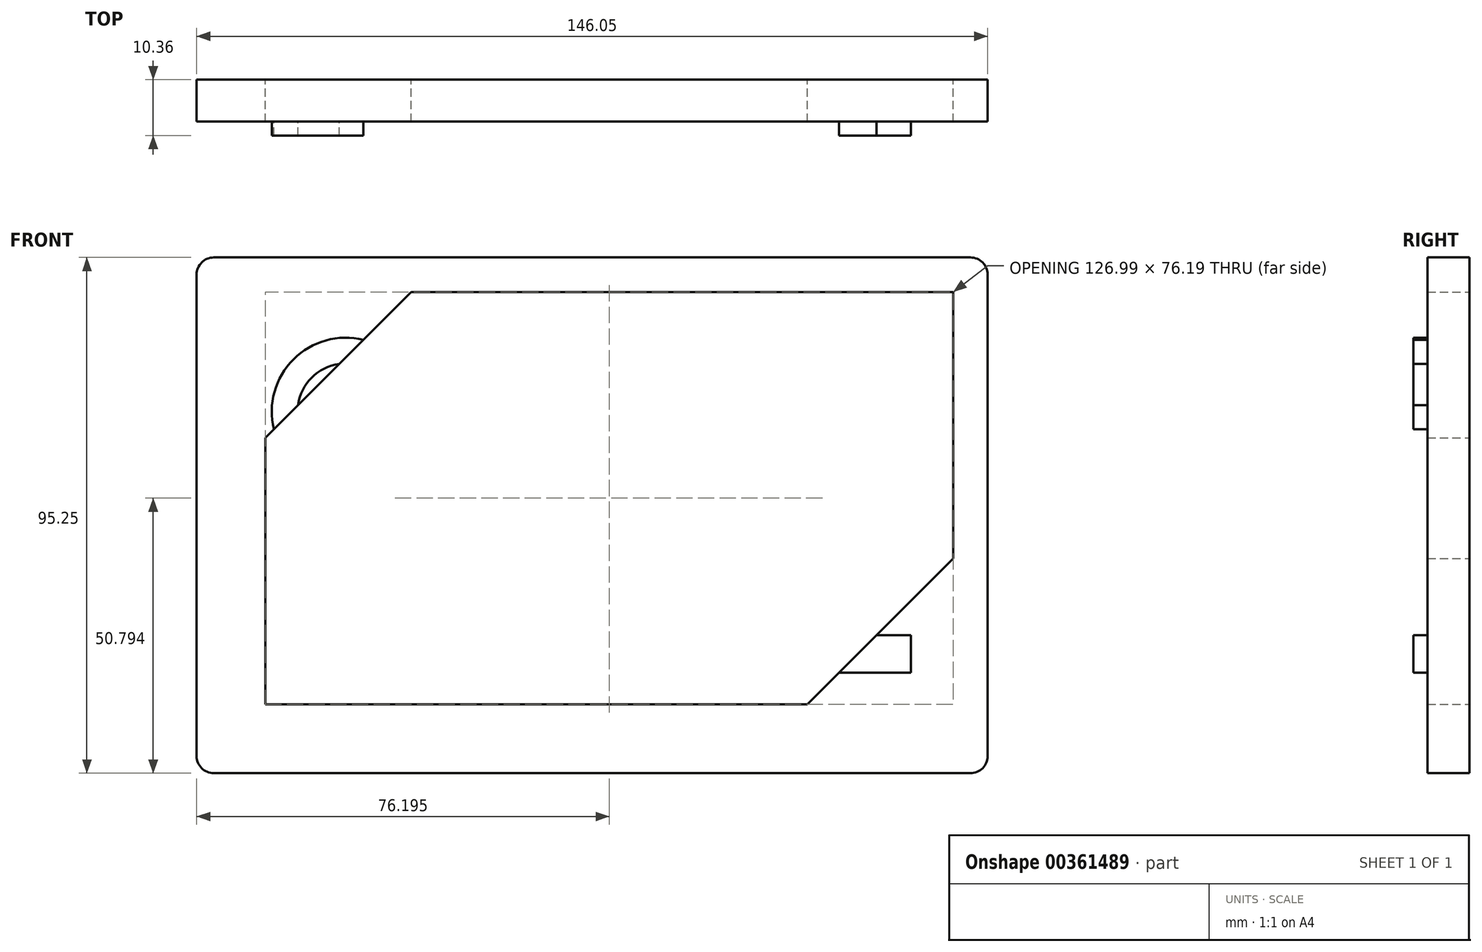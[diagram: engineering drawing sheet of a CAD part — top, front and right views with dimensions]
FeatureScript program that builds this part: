
annotation { "Feature Type Name" : "Feature", "Feature Type Description" : "" }
export const myFeature = defineFeature(function(context is Context, id is Id, definition is map)
    precondition{}
    {
        {
            var Q0;
            Q0=qCreatedBy(makeId("Front.planeOp"),FACE);
            var sketch = newSketch(context, id + "F0", { "sketchPlane" : qUnion([Q0])});
            skArc(sketch, "E0", {"start": v(-36.47, 6.36) * mm, "mid": v(-38.71, 5.43) * mm, "end": v(-39.64, 3.18) * mm});
            skArc(sketch, "E1", {"start": v(106.4, 3.18) * mm, "mid": v(105.48, 5.43) * mm, "end": v(103.23, 6.36) * mm});
            skArc(sketch, "E2", {"start": v(-39.64, -85.72) * mm, "mid": v(-38.71, -87.96) * mm, "end": v(-36.47, -88.9) * mm});
            skArc(sketch, "E3", {"start": v(103.23, -88.9) * mm, "mid": v(105.48, -87.96) * mm, "end": v(106.4, -85.72) * mm});
            skLineSegment(sketch, "E4", {"start": v(-39.64, 3.18) * mm, "end": v(-39.64, -85.72) * mm});
            skLineSegment(sketch, "E5", {"start": v(-36.47, -88.9) * mm, "end": v(103.23, -88.9) * mm});
            skLineSegment(sketch, "E6", {"start": v(106.4, -85.72) * mm, "end": v(106.4, 3.18) * mm});
            skLineSegment(sketch, "E7", {"start": v(-36.47, 6.36) * mm, "end": v(103.23, 6.36) * mm});
            skLineSegment(sketch, "E8", {"start": v(-26.94, -76.2) * mm, "end": v(73.1, -76.2) * mm});
            skLineSegment(sketch, "E9", {"start": v(73.1, -76.2) * mm, "end": v(100.05, -49.25) * mm});
            skLineSegment(sketch, "E10", {"start": v(100.05, -49.25) * mm, "end": v(100.05, 0) * mm});
            skLineSegment(sketch, "E11", {"start": v(100.05, 0) * mm, "end": v(0, 0) * mm});
            skLineSegment(sketch, "E12", {"start": v(0, 0) * mm, "end": v(-26.94, -26.94) * mm});
            skLineSegment(sketch, "E13", {"start": v(-26.94, -26.94) * mm, "end": v(-26.94, -76.2) * mm});
            skSolve(sketch);
        }
        {
            var Q0;
            {var subQ1=sQuery(id+"F0.wireOp",EDGE,"E0");Q0=makeQuery(id+"F0.imprint","IMPRINT",FACE,{"disambiguationData":[TD([[makeQuery(id+"F0.imprint","IMPRINT",EDGE,{"derivedFrom":subQ1}),1.0]])]});}
            extrude(context, id + "F1", {"entities" : qUnion([Q0]), "depth" : 7.77 * mm});
        }
        {
            var Q0;
            Q0=makeQuery(id+"F1.opExtrude","CAP_FACE",FACE,{"disambiguationData":[OSD([sQuery(id+"F0.wireOp",EDGE,"E0"),sQuery(id+"F0.wireOp",EDGE,"E1"),sQuery(id+"F0.wireOp",EDGE,"E2"),sQuery(id+"F0.wireOp",EDGE,"E3"),sQuery(id+"F0.wireOp",EDGE,"E4"),sQuery(id+"F0.wireOp",EDGE,"E5"),sQuery(id+"F0.wireOp",EDGE,"E6"),sQuery(id+"F0.wireOp",EDGE,"E7"),sQuery(id+"F0.wireOp",EDGE,"E8"),sQuery(id+"F0.wireOp",EDGE,"E9"),sQuery(id+"F0.wireOp",EDGE,"E10"),sQuery(id+"F0.wireOp",EDGE,"E11"),sQuery(id+"F0.wireOp",EDGE,"E12"),sQuery(id+"F0.wireOp",EDGE,"E13")])],"isStart":false});
            var sketch = newSketch(context, id + "F2", { "sketchPlane" : qUnion([Q0])});
            skCircle(sketch, "E14", {"center": v(-12.1, -22.12) * mm, "radius": 13.67 * mm});
            skCircle(sketch, "E15", {"center": v(-12.1, -22.12) * mm, "radius": 8.9 * mm});
            skLineSegment(sketch, "E16.bottom", {"start": v(85.9, -63.4) * mm, "end": v(92.26, -63.4) * mm});
            skLineSegment(sketch, "E16.top", {"start": v(78.98, -70.33) * mm, "end": v(92.26, -70.33) * mm});
            skLineSegment(sketch, "E16.right", {"start": v(92.26, -63.4) * mm, "end": v(92.26, -70.33) * mm});
            skLineSegment(sketch, "E17", {"start": v(78.98, -70.33) * mm, "end": v(85.9, -63.4) * mm});
            skSolve(sketch);
        }
        {
            var Q0;
            Q0=makeQuery(id+"F2.imprint","IMPRINT",FACE,{"disambiguationData":[TD([[makeQuery(id+"F2.imprint","IMPRINT",EDGE,{"derivedFrom":sQuery(id+"F2.wireOp",EDGE,"E16.bottom")}),-1.0]])]});
            var Q1;
            {var subQ0=sQuery(id+"F2.wireOp",EDGE,"E14");var subQ1=makeQuery(id+"F1.opExtrude","CAP_EDGE",EDGE,{"disambiguationData":[OSD([sQuery(id+"F0.wireOp",EDGE,"E12")])],"isStart":false});var subQ2=makeQuery(id+"F2.imprint","INTERSECT",VERTEX,{"disambiguationData":[OD(0.0)],"derivedFrom":[subQ1,subQ0]});Q1=makeQuery(id+"F2.imprint","IMPRINT",FACE,{"disambiguationData":[TD([[makeQuery(id+"F2.imprint","IMPRINT",EDGE,{"disambiguationData":[TD([[subQ2,-1.0]])],"derivedFrom":subQ0}),1.0]])]});}
            extrude(context, id + "F3", {"entities" : qUnion([Q0, Q1]), "operationType" : NewBodyOperationType.ADD, "depth" : 2.6 * mm});
        }
    });
